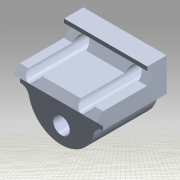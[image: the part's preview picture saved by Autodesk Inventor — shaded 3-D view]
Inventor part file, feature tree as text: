
AUTODESK INVENTOR PART (.ipt)
format: ipt  version: 2018 (Build 220112000, 112)  size: 157,184 bytes
history: native  units: mm (DEFAULTED — no unit token found)
features: sketch x3, extrude x2, fillet x1, projected_geometry x1, chamfer x1
ambient origin geometry x8: Origin, YZ Plane, XZ Plane, XY Plane, X Axis, Y Axis, Z Axis, Center Point
bodies: Solid1 (feature_tree)
feature tree (8):
  extrude  "Extrusion1"  Depth=25.4mm
  sketch  "Sketch2"  dims[d5=6.35mm d6=25.4mm d7=0.0mm d8=3.175mm]
  extrude  "Extrusion2"  Depth=25.4mm TaperAngle=0.0deg
  fillet  "Fillet1"  Radius=3.175mm
  sketch  "Sketch1"  dims[d0=76.2mm d1=38.1mm d2=0.0mm d3=0.0mm d4=25.4mm]
  projected_geometry  "Projected Loop1"
  sketch  "Sketch3"
  chamfer  "Chamfer1"  [1 undecoded]
note: 1 required parameter value undecoded (feature->parameter linkage not recoverable at this tier; creation-order binding heuristic only, values carry confidence <= 0.55)
